# Revit family: Угольник равнопроходной ВР
name_source: partatom
category: Соединительные детали трубопроводов
revit_build: Autodesk Revit 2017 (Build: 20160225_1515(x64)
units: mm (PartAtom-declared; Revit-internal decimal feet)

## family parameters
Всегда вертикально = Да
На основе рабочей плоскости = Нет
Общий = Нет
При загрузке вырезать с полостями = Нет
Размер круглого соединителя = Использовать радиус
Тип детали = Отвод

## types (2) — shared parameters
ADSK_Единица измерения = шт
ADSK_Завод-изготовитель = ООО САНЕКСТ.ПРО
ADSK_Материал наименование = DZR латунь
ADSK_Расход жидкости = 0.0 л/с
URL = http://sanext.ru
Изготовитель = ООО САНЕКСТ.ПРО
Материал фитинга = DZR латунь
Описание = Угольник равнопроходной ВР
Разработчик = ООО ПРОРУБИМ
Разработчик (телефон) = +7(495)649-85-43
Разработчик модели (URL) = http://prorubim.com
Таблица_артикул = Угольник равнопроходной ВР артикул
Таблица_наименование = Угольник равнопроходной ВР
zero-valued in all types: ADSK_Масса

## type names (no varying parameters)
- Тип
- Угольник равнопроходной ВР
